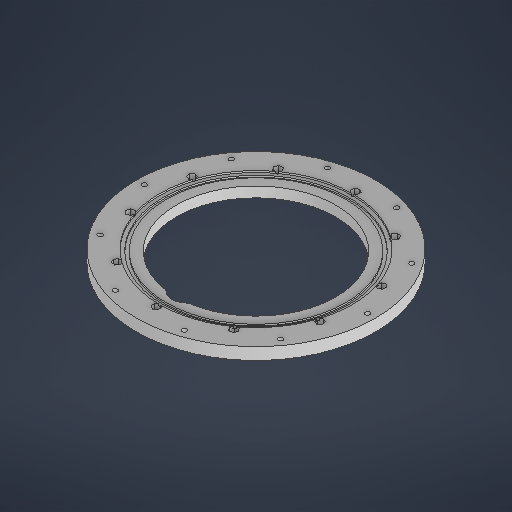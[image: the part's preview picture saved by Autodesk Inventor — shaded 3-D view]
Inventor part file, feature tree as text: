
AUTODESK INVENTOR PART (.ipt)
format: ipt  version: 2025 (Build 290162000, 162)  size: 553,984 bytes
history: native  units: in
note: dims shown in document units (in); Inventor stores cm internally (conversion verified against a paired STEP export)
features: sketch x12, extrude x6, plane x2, hole x1, revolve x1
ambient origin geometry x8: Origin, YZ Plane, XZ Plane, XY Plane, X Axis, Y Axis, Z Axis, Center Point
bodies: Solid1 (feature_tree)
feature tree (22):
  sketch  "Sketch1"  dims[d0=11.811in d1=7.874in]
  extrude  "Extrusion1"  Depth=7.874in
  sketch  "Sketch2"  dims[d7=0.2343in d9=3.937in d11=360.0deg]
  extrude  "Extrusion2"  Depth=0.1969in TaperAngle=0.0deg
  sketch  "Sketch3"  dims[d13=0.3012in d14=0.0in d15=9.8425in]
  extrude  "Extrusion3"  Depth=3.937in TaperAngle=360.0deg
  extrude  "Extrusion6"  Depth=9.8425in
  extrude  "Extrusion7"  Depth=0.1575in TaperAngle=0.0deg
  hole  "Hole2"  [1 undecoded]
  revolve  "Revolution1"  [1 undecoded]
  plane  "Work Plane3"
  plane  "Work Plane4"
  extrude  "Extrusion12"  Depth=0.1575in
  sketch  "Sketch Circular Pattern1"  dims[d2=9.8425in d5=0.1969in d6=0.0in]
  sketch  "Sketch5"  dims[d29=9.5079in d30=0.0837in d31=0.0in]
  sketch  "Sketch6"  dims[d47=3.937in d49=360.0deg]
  sketch  "Sketch8"  dims[d59=0.1575in]
  sketch  "Sketch Circular Pattern4"  dims[d20=0.1319in d21=0.0in d27=0.1575in d28=0.0in]
  sketch  "Sketch9"  dims[d60=0.5709in]
  sketch  "Sketch Circular Pattern5"  dims[d45=11.0236in d46=0.2165in]
  sketch  "Sketch Circular Pattern6"  dims[d51=0.2343in d52=0.2362in d53=0.4124in d54=0.2904in d55=90.0deg d56=0.315in d57=0.8108in d58=0.1575in]
  sketch  "Sketch13"  dims[d61=0.1575in d62=0.1575in d63=90.0deg d64=0.3445in d65=4.9213in d66=4.9213in d67=0.3445in d70=3.937in d72=360.0deg d74=3.937in d76=360.0deg d78=7.874in d79=7.874in d91=2.5in d92=1.5748in d93=3.2245in d94=10.0812in d95=0.0in d25=0.0197in d26=0.0344in]
note: 2 required parameter values undecoded (feature->parameter linkage not recoverable at this tier; creation-order binding heuristic only, values carry confidence <= 0.55)